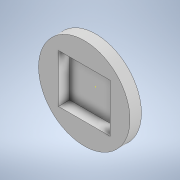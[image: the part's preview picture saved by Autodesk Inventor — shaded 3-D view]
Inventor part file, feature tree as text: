
AUTODESK INVENTOR PART (.ipt)
format: ipt  version: 2021 (Build 250183000, 183)  size: 292,352 bytes
history: native  units: in
note: dims shown in document units (in); Inventor stores cm internally (conversion verified against a paired STEP export)
features: sketch x6, extrude x5, projected_geometry x4, pattern_linear x2, plane x1, mirror x1
ambient origin geometry x8: Origin, YZ Plane, XZ Plane, XY Plane, X Axis, Y Axis, Z Axis, Center Point
bodies: Body1 (feature_tree)
feature tree (19):
  sketch  "Sketch1"  dims[d0=1.1295in d1=1.06in]
  plane  "Work Plane1"
  extrude  "Extrusion2"  Depth=1.06in
  extrude  "Extrusion3"  Depth=0.25in TaperAngle=0.0deg
  extrude  "Extrusion4"  Depth=0.006in TaperAngle=0.0deg
  pattern_linear  "Rectangular Pattern1"  Count1=12 Spacing1=0.1in
  extrude  "Extrusion5"  Depth=0.006in TaperAngle=0.0deg
  extrude  "Extrusion6"  TaperAngle=0.0deg  [1 undecoded]
  pattern_linear  "Rectangular Pattern2"  Count1=6 Spacing1=0.2in
  mirror  "Mirror1"
  sketch  "Sketch6"
  sketch  "Sketch2"  dims[d4=2.0in d5=0.25in d6=0.0in]
  sketch  "Sketch3"  dims[d7=0.25in d8=0.0in d10=0.006in d11=0.0in d12=4.7244in d14=0.1in]
  projected_geometry  "Projected Loop1"
  projected_geometry  "Projected Loop2"
  sketch  "Sketch4"  dims[d15=0.01in d16=0.006in d17=0.0in]
  projected_geometry  "Projected Loop3"
  sketch  "Sketch5"  dims[d18=0.0394in d20=0.0in d21=0.0in d22=2.3622in d24=0.2in]
  projected_geometry  "Projected Loop4"
note: 1 required parameter value undecoded (feature->parameter linkage not recoverable at this tier; creation-order binding heuristic only, values carry confidence <= 0.55)
